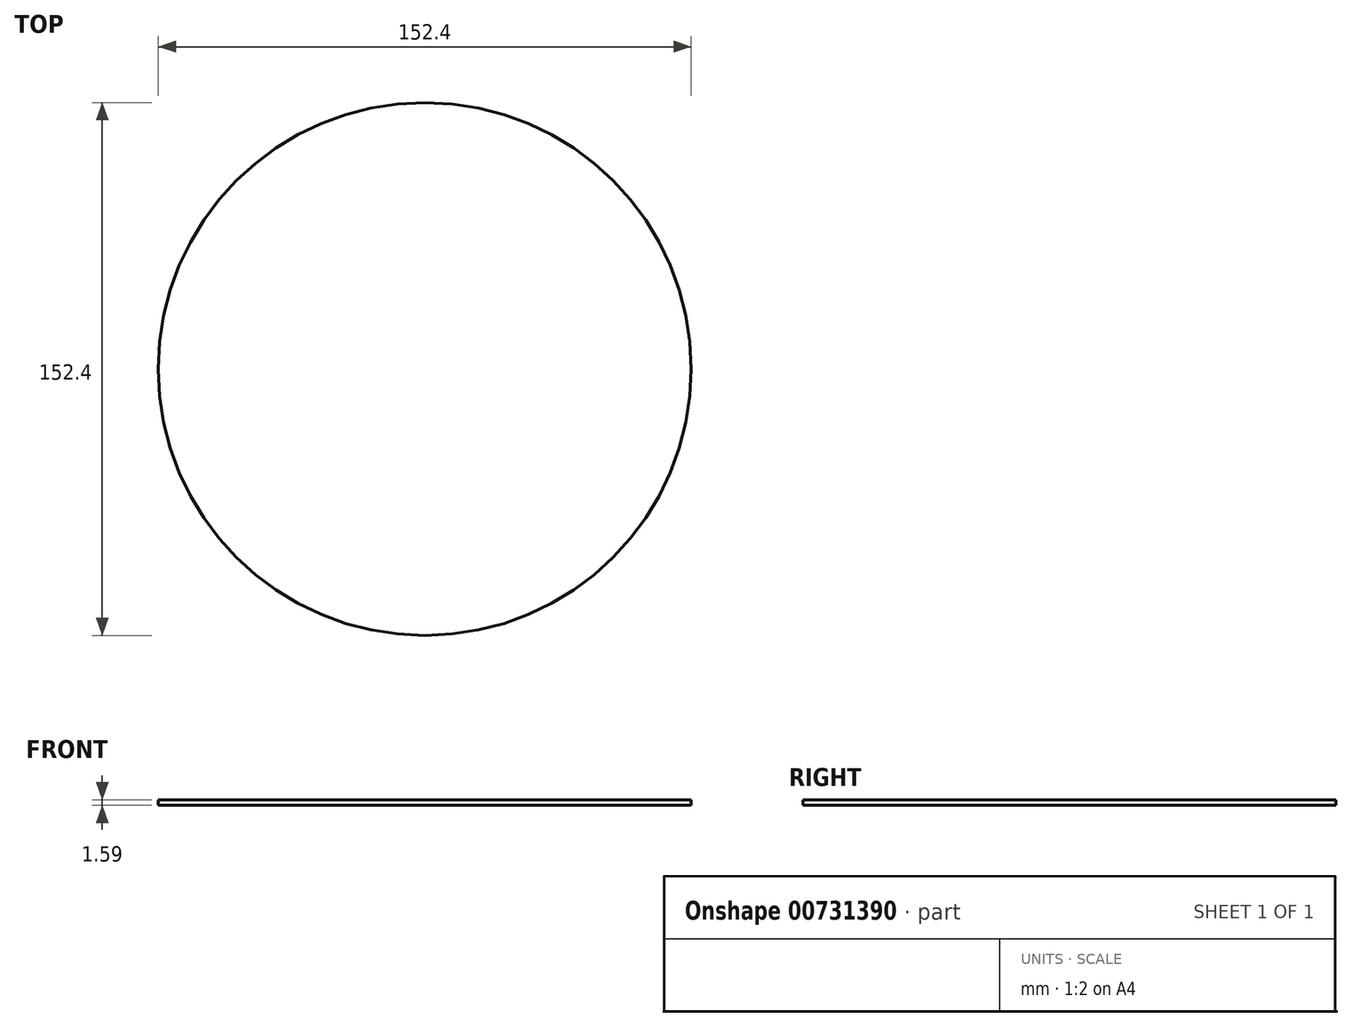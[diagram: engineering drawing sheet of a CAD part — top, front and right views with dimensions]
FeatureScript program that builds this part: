
annotation { "Feature Type Name" : "Feature", "Feature Type Description" : "" }
export const myFeature = defineFeature(function(context is Context, id is Id, definition is map)
    precondition{}
    {
        {
            var Q0;
            Q0=qCreatedBy(makeId("Top.planeOp"),FACE);
            var sketch = newSketch(context, id + "F0", { "sketchPlane" : qUnion([Q0])});
            skCircle(sketch, "E0", {"center": v(0, 0) * mm, "radius": 76.2 * mm});
            skSolve(sketch);
        }
        {
            var Q0;
            Q0 = qSketchRegion(id + "F0", true);
            extrude(context, id + "F1", {"entities" : qUnion([Q0]), "depth" : 1.59 * mm, "offsetDistance" : 25.4 * mm});
        }
    });
